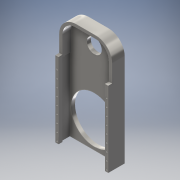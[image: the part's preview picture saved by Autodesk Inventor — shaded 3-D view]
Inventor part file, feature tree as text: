
AUTODESK INVENTOR PART (.ipt)
format: ipt  version: 2016 (Build 200138000, 138)  size: 380,416 bytes
history: native  units: mm
features: sketch x14, extrude x12, reference x8, projected_geometry x7, hole x5, other x1, chamfer x1, plane x1
ambient origin geometry x8: Origin, YZ Plane, XZ Plane, XY Plane, X Axis, Y Axis, Z Axis, Center Point
bodies: Solid1 (feature_tree)
feature tree (49):
  other  "Cup_Dispenser_Slider.ipt"
  sketch  "Sketch2"  dims[d0=10.0mm d1=82.0mm]
  extrude  "Extrusion1"  Depth=82.0mm
  hole  "Hole1"  [1 undecoded]
  extrude  "Extrusion2"  Depth=6.0mm
  chamfer  "Chamfer1"  Distance=6.0mm
  extrude  "Extrusion4"  Depth=19.5mm TaperAngle=0.0deg
  extrude  "Extrusion13"  Depth=2.0mm TaperAngle=45.0deg
  extrude  "Extrusion14"  Depth=3.0mm
  extrude  "Extrusion15"  Depth=6.0mm TaperAngle=0.0deg
  hole  "Hole6"  [1 undecoded]
  extrude  "Extrusion16"  Depth=3.0mm
  extrude  "Extrusion17"  Depth=6.0mm
  extrude  "Extrusion18"  Depth=4.0mm
  hole  "Hole7"  [1 undecoded]
  extrude  "Extrusion9"  Depth=3.0mm TaperAngle=0.0deg
  extrude  "Extrusion10"  Depth=3.0mm TaperAngle=0.0deg
  hole  "Hole3"  [1 undecoded]
  plane  "Work Plane2"
  hole  "Hole4"  [1 undecoded]
  extrude  "Extrusion12"  Depth=3.0mm TaperAngle=0.0deg
  sketch  "Sketch13"  dims[d4=70.0mm d5=70.0mm d6=6.0mm d7=0.0mm]
  sketch  "Sketch4"  dims[d2=117.0mm d3=3.0mm]
  projected_geometry  "Projected Loop1"
  sketch  "Sketch16"  dims[d8=72.0mm d9=19.5mm d10=0.0mm]
  reference  "Reference15"
  reference  "Reference16"
  reference  "Reference17"
  reference  "Reference18"
  reference  "Reference19"
  sketch  "Sketch18"  dims[d13=3.0mm d14=6.0mm d15=4.0mm d16=2.0mm d17=90.0deg d18=4.0mm d19=20.594885mm d20=2.0mm d21=2.0mm d22=45.0deg]
  sketch  "Sketch21"  dims[d23=3.0mm d24=0.0mm d60=31.0mm]
  projected_geometry  "Projected Loop7"
  sketch  "Sketch22"  dims[d61=31.0mm d64=6.0mm d65=0.0mm]
  projected_geometry  "Projected Loop8"
  sketch  "Sketch23"  dims[d66=35.0mm d67=23.0mm]
  projected_geometry  "Projected Loop9"
  sketch  "Sketch24"  dims[d68=3.0mm d69=23.0mm]
  sketch  "Sketch25"  dims[d70=3.0mm d71=0.0mm]
  sketch  "Sketch26"  dims[d72=3.0mm d73=6.0mm d74=4.0mm d75=2.0mm d76=90.0deg d77=4.0mm d78=20.594885mm d81=6.0mm]
  projected_geometry  "Projected Loop10"
  sketch  "Sketch28"  dims[d82=3.0mm d83=6.0mm d84=4.0mm d85=2.0mm d86=90.0deg d87=4.0mm d88=20.594885mm d96=24.0mm]
  reference  "Reference27"
  reference  "Reference28"
  sketch  "Sketch29"  dims[d97=48.0mm d99=2.0mm d100=0.0mm]
  sketch  "Sketch30"  dims[d101=6.0mm d102=0.0mm d103=3.0mm d104=0.0mm d105=3.0mm d106=0.0mm d107=31.0mm d108=31.0mm d109=3.0mm d110=6.0mm d111=4.0mm d112=2.0mm d113=90.0deg d114=4.0mm d115=20.594885mm d116=3.0mm d117=0.0mm d123=3.0mm d124=0.0mm d125=60.0mm d126=30.0mm d127=3.0mm d128=2.0mm d129=0.0mm d130=3.0mm d131=90.0mm d133=12.0mm d134=10.0mm d136=10.0mm d138=2.0mm d139=6.0mm d140=4.0mm d141=2.0mm d142=90.0deg d143=4.0mm d144=20.594885mm d148=45.0deg d150=3.0mm d152=5.0mm d154=45.0deg]
  projected_geometry  "Projected Loop12"
  projected_geometry  "Projected Loop14"
  reference  "Reference34"
note: 5 required parameter values undecoded (feature->parameter linkage not recoverable at this tier; creation-order binding heuristic only, values carry confidence <= 0.55)
